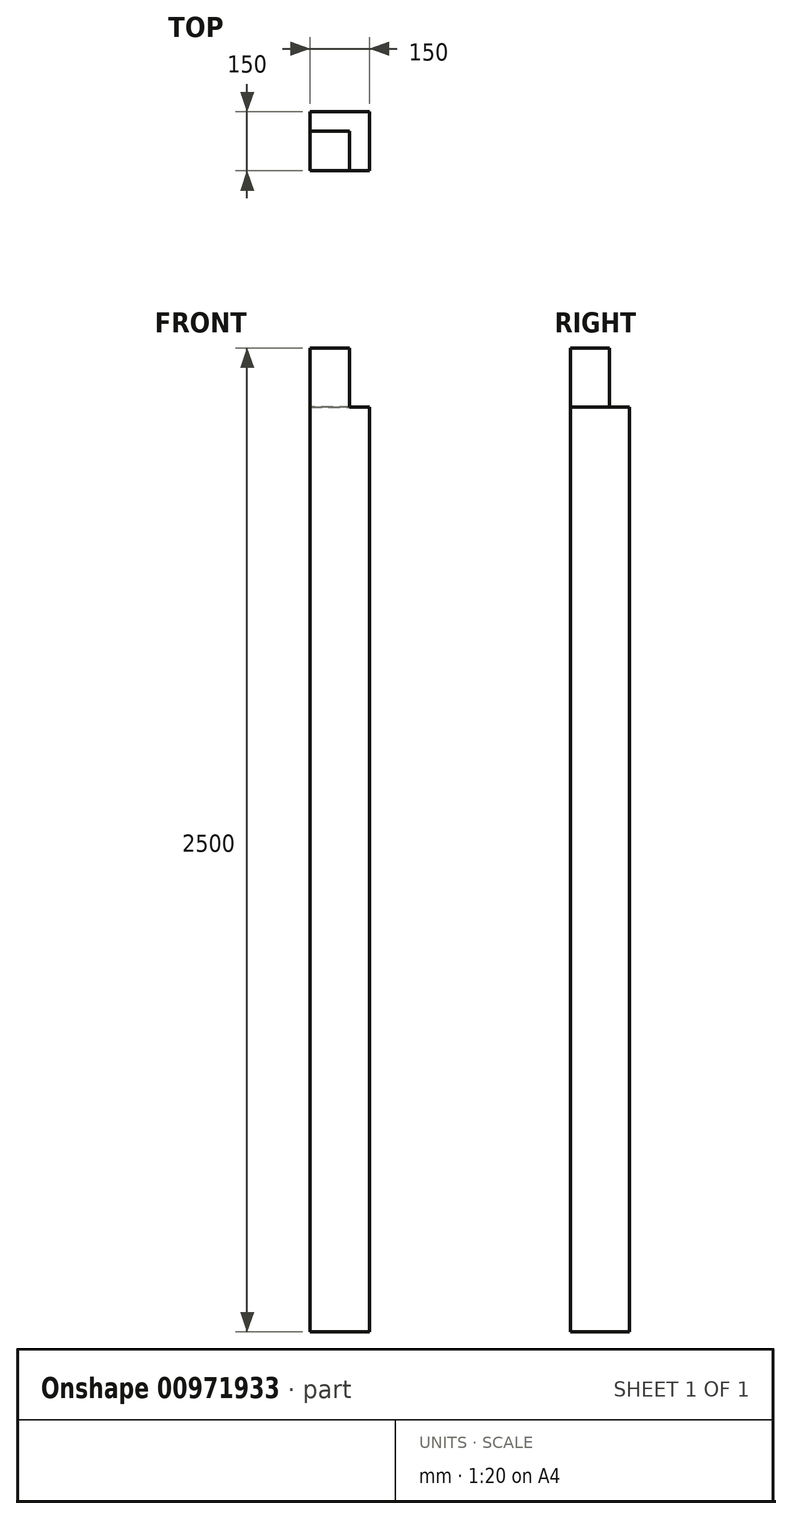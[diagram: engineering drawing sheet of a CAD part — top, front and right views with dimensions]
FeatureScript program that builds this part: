
annotation { "Feature Type Name" : "Feature", "Feature Type Description" : "" }
export const myFeature = defineFeature(function(context is Context, id is Id, definition is map)
    precondition{}
    {
        {
            var Q0;
            Q0=qCreatedBy(makeId("Top.planeOp"),FACE);
            var sketch = newSketch(context, id + "F0", { "sketchPlane" : qUnion([Q0])});
            skLineSegment(sketch, "E0.bottom", {"start": v(75, -75) * mm, "end": v(-75, -75) * mm});
            skLineSegment(sketch, "E0.top", {"start": v(75, 75) * mm, "end": v(-75, 75) * mm});
            skLineSegment(sketch, "E0.left", {"start": v(75, -75) * mm, "end": v(75, 75) * mm});
            skLineSegment(sketch, "E0.right", {"start": v(-75, -75) * mm, "end": v(-75, 75) * mm});
            skPoint(sketch, "E0.middle", {"position": v(0, 0) * mm});
            skSolve(sketch);
        }
        {
            var Q0;
            Q0=makeQuery(id+"F0.imprint","IMPRINT",FACE,{"disambiguationData":[TD([[makeQuery(id+"F0.imprint","IMPRINT",EDGE,{"derivedFrom":sQuery(id+"F0.wireOp",EDGE,"E0.bottom")}),-1.0]])]});
            extrude(context, id + "F1", {"entities" : qUnion([Q0]), "depth" : 2500 * mm, "offsetDistance" : 25 * mm});
        }
        {
            var Q0;
            Q0=makeQuery(id+"F1.opExtrude","CAP_FACE",FACE,{"disambiguationData":[OSD([sQuery(id+"F0.wireOp",EDGE,"E0.bottom"),sQuery(id+"F0.wireOp",EDGE,"E0.top"),sQuery(id+"F0.wireOp",EDGE,"E0.left"),sQuery(id+"F0.wireOp",EDGE,"E0.right")])],"isStart":false});
            var sketch = newSketch(context, id + "F2", { "sketchPlane" : qUnion([Q0])});
            skLineSegment(sketch, "E1", {"start": v(25, -75) * mm, "end": v(75, -75) * mm});
            skLineSegment(sketch, "E2", {"start": v(75, -75) * mm, "end": v(75, 75) * mm});
            skLineSegment(sketch, "E3", {"start": v(75, 75) * mm, "end": v(-75, 75) * mm});
            skLineSegment(sketch, "E4", {"start": v(-75, 75) * mm, "end": v(-75, 25) * mm});
            skLineSegment(sketch, "E5", {"start": v(-75, 25) * mm, "end": v(25, 25) * mm});
            skLineSegment(sketch, "E6", {"start": v(25, 25) * mm, "end": v(25, -75) * mm});
            skSolve(sketch);
        }
        {
            var Q0;
            Q0 = qSketchRegion(id + "F2", true);
            extrude(context, id + "F3", {"entities" : qUnion([Q0]), "operationType" : NewBodyOperationType.REMOVE, "oppositeDirection" : true, "depth" : 150 * mm, "offsetDistance" : 25 * mm});
        }
    });
